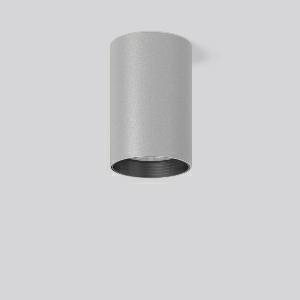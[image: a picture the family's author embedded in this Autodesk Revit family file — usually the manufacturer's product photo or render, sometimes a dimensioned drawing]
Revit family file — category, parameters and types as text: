
# Revit family: heledon_maxi_a_931220_004_3_76_072a
name_source: partatom
category: Lighting Fixtures
units: mm (PartAtom-declared; Revit-internal decimal feet)

## family parameters
Cut with Voids When Loaded = No
Host = Face
Light Source = No
Part Type = Normal
Room Calculation Point = No
Round Connector Dimension = Use Diameter
Shared = No

## types (1)
- HELEDON maxi A (1 x LED Modul 935, 2900 lm, 3500)
    Apparent Load = 25 VA
    Approval mark = CE
    CIE Flux Codes = 97 100 100 100 100
    Color Rendering = 92
    Color Temperature = 3500
    Default Elevation = 1800 mm
    Description = Series: HELEDON maxi
Cylindrical surface-mounted downlight. Housing: die-cast aluminium, powder-coated. Internal ceiling frame polycarbonate with bayonet mounting. Black plastic ring and recessed LED to prevent glare from the side. Optical assembly with lens made of plastic (polycarbonate) for the best homogeneous light distribution - can be changed without tools. Best colour rendering index Ra>90. Suitable for Ceiling mounting. Easy installation with a separate ceiling frame with bayonet mounting and plug connection. Driver integrated. Connected via plug-in connector. High quality converter without flickering and stroboscopic effect. The following accessories can be mounted without use of tools: interchangeable lenses, decorative glasses, honeycomb louvre, clear and frosted diffusers, white interchangeable plastic ring. 
Colour: silver
Diameter: 123 mm
Height: 183 mm
Lamp: LED
Socket: without socket
Colour temperature: 3500K
Colour rendering index (CRI): 92
System power: 25 W
Rated luminous flux: 2900 lm
Luminous efficiency: 116 lm/W
Control gear: Converter, dimmable, DALI
Protection class: I
Type of protection: IP 20
    Height = 183 mm
    Lamp = 1 x LED Modul 935
    Lamp Light Flux = 2900 lm
    Lamp count = 1
    Length = 123 mm
    Lifetime = 50000 h
    Luminous efficacy = 116 lm/W
    Manufacturer = RZB
    ModVariant = No
    Model = 931220.004.3.76
    Mounting Place = Ceiling
    Mounting Type = Surface mounted
    Number of Poles = 1
    OnlyDefault = Yes
    Power Factor = 1
    Product Name = HELEDON maxi A
    Product group = Surface mounted downlights
    ProductGroupID = 302
    Protection Class = Protection class I
    Protection Degree = IP 20
    RLX_Detail_Level = 1
    RLX_Emergency_Light_Flux = 0 lm
    RLX_Emergency_Type = 0
    RLX_Emergency_Type_DB = No
    RlxData = <blob elided: 98481 chars, md5=a5829bdf>
    Socket = socket
    Standby Power = 0 W
    System Light Flux = 2900 lm
    System Power = 25 W
    Type Comments = Product without accessories
    Type Image = 931193.004.jpg
    URL = http://relux.com
    VarID = ---
    Voltage = 230 V
    Voltage Range = 220-240 V
    Weight = 0.00 kg
    Width = 0 mm  [stored 0 ft]

note: [stored X ft] marks values corroborated as IEEE doubles in the binary element streams (Revit-internal decimal feet)

## geometry (parser evidence)
native form markers: Blend x4, Sweep x8
no freeform markers — native parametric forms only
